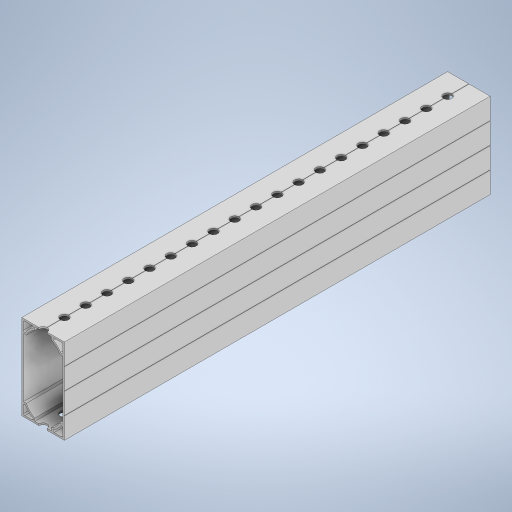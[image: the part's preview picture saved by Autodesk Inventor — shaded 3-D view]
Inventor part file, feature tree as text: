
AUTODESK INVENTOR PART (.ipt)
format: ipt  version: 2023 (Build 270158000, 158)  size: 739,840 bytes
history: native  units: in
note: dims shown in document units (in); Inventor stores cm internally (conversion verified against a paired STEP export)
features: extrude x1, sketch x1, other x1
ambient origin geometry x8: Origin, YZ Plane, XZ Plane, XY Plane, X Axis, Y Axis, Z Axis, Center Point
bodies: Solid1 (feature_tree)
feature tree (3):
  extrude  "Extrusion1"  [1 undecoded]
  sketch  "Sketch1"  dims[d0=37.0in d1=0.0in]
  other  "Scribe Line Pattern"
note: 1 required parameter value undecoded (feature->parameter linkage not recoverable at this tier; creation-order binding heuristic only, values carry confidence <= 0.55)
